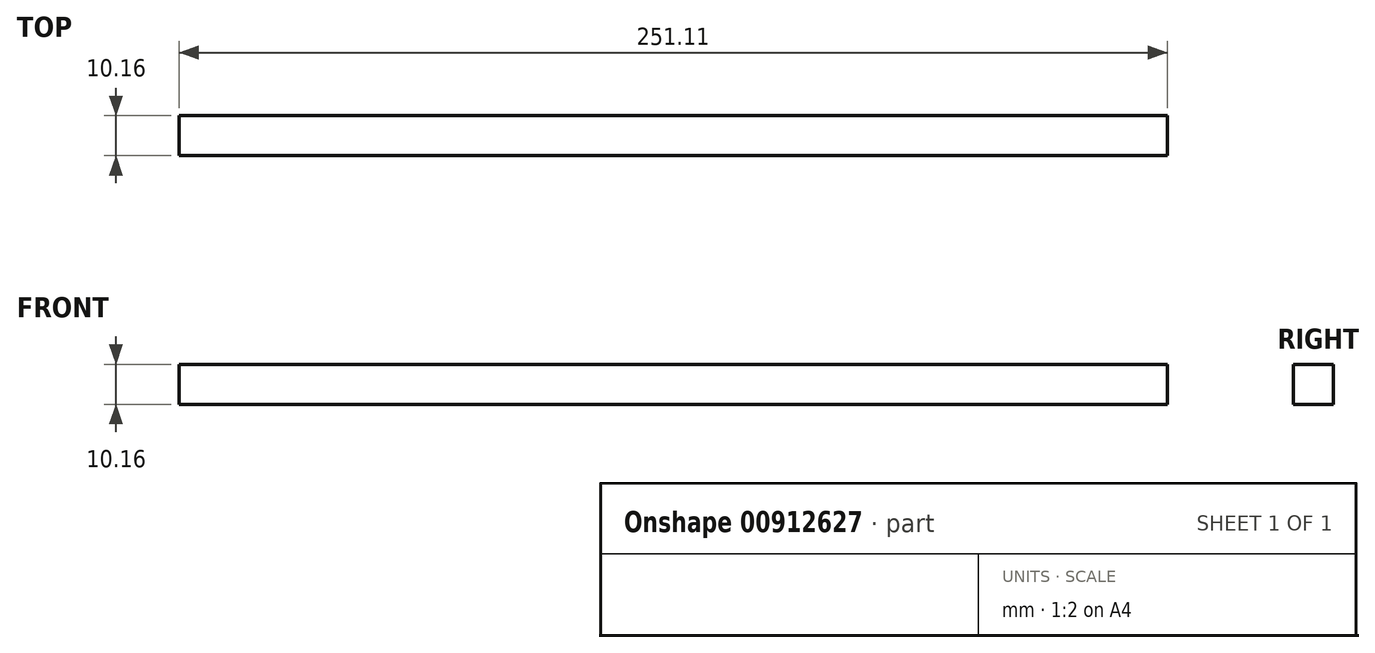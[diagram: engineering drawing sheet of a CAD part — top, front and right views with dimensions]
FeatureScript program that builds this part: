
annotation { "Feature Type Name" : "Feature", "Feature Type Description" : "" }
export const myFeature = defineFeature(function(context is Context, id is Id, definition is map)
    precondition{}
    {
        {
            var Q0;
            Q0=qCreatedBy(makeId("Top.planeOp"),FACE);
            var sketch = newSketch(context, id + "F0", { "sketchPlane" : qUnion([Q0])});
            skLineSegment(sketch, "E0", {"start": v(-147.98, 0) * mm, "end": v(103.13, 0) * mm});
            skLineSegment(sketch, "E1", {"start": v(-147.98, 0) * mm, "end": v(-147.98, -10.16) * mm});
            skLineSegment(sketch, "E2", {"start": v(103.13, 0) * mm, "end": v(103.13, -10.16) * mm});
            skLineSegment(sketch, "E3", {"start": v(-147.98, -10.16) * mm, "end": v(103.13, -10.16) * mm});
            skSolve(sketch);
        }
        {
            var Q0;
            Q0=makeQuery(id+"F0.imprint","IMPRINT",FACE,{"disambiguationData":[TD([[makeQuery(id+"F0.imprint","IMPRINT",EDGE,{"derivedFrom":sQuery(id+"F0.wireOp",EDGE,"E0")}),-1.0]])]});
            extrude(context, id + "F1", {"entities" : qUnion([Q0]), "depth" : 10.16 * mm, "offsetDistance" : 25.4 * mm});
        }
    });
